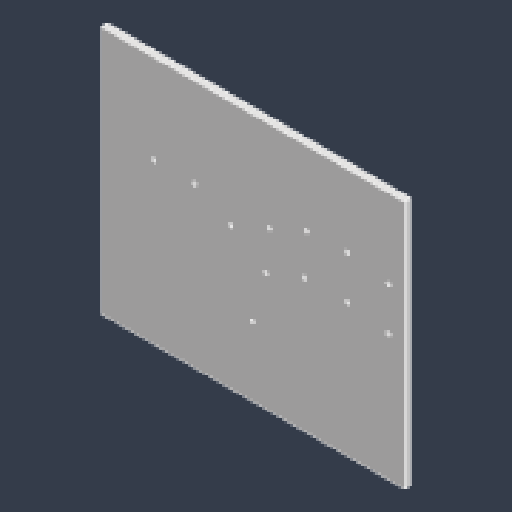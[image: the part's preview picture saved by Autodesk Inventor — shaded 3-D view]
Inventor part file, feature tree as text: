
AUTODESK INVENTOR PART (.ipt)
format: ipt  version: 2023.4 (Build 274418000, 418)  size: 294,400 bytes
history: native  units: mm
features: sketch x4, extrude x3, projected_geometry x2, hole x1
ambient origin geometry x8: Origin, YZ Plane, XZ Plane, XY Plane, X Axis, Y Axis, Z Axis, Center Point
bodies: Solid1 (feature_tree)
feature tree (10):
  extrude  "Extrusion1"  Depth=180.0mm
  hole  "Hole1"  [1 undecoded]
  extrude  "Extrusion2"  Depth=26.3mm
  extrude  "Extrusion3"  Depth=52.4mm
  sketch  "Sketch1"  dims[d0=220.0mm d1=180.0mm]
  sketch  "Sketch2"  dims[d3=0.0mm d4=50.4mm]
  sketch  "Sketch3"  dims[d5=15.5mm d6=26.3mm]
  projected_geometry  "Projected Loop1"
  sketch  "Sketch4"  dims[d7=29.5mm d11=52.4mm d12=65.3mm d13=65.2mm d14=9.7mm d15=29.4mm d16=2.6mm d17=26.9mm d18=29.6mm d19=29.5mm d20=1.7mm d22=46.0mm d23=30.1mm d24=96.7mm d25=91.7mm d26=31.0mm d27=31.0mm d28=35.0mm d29=3.0mm d30=6.0mm d31=3.6mm d32=2.0mm d33=90.0deg d34=8.0mm d35=20.594885mm d36=14.0mm d44=0.0mm d45=0.0mm d46=15.2mm d50=3.6mm d51=0.0mm]
  projected_geometry  "Projected Loop2"
note: 1 required parameter value undecoded (feature->parameter linkage not recoverable at this tier; creation-order binding heuristic only, values carry confidence <= 0.55)
